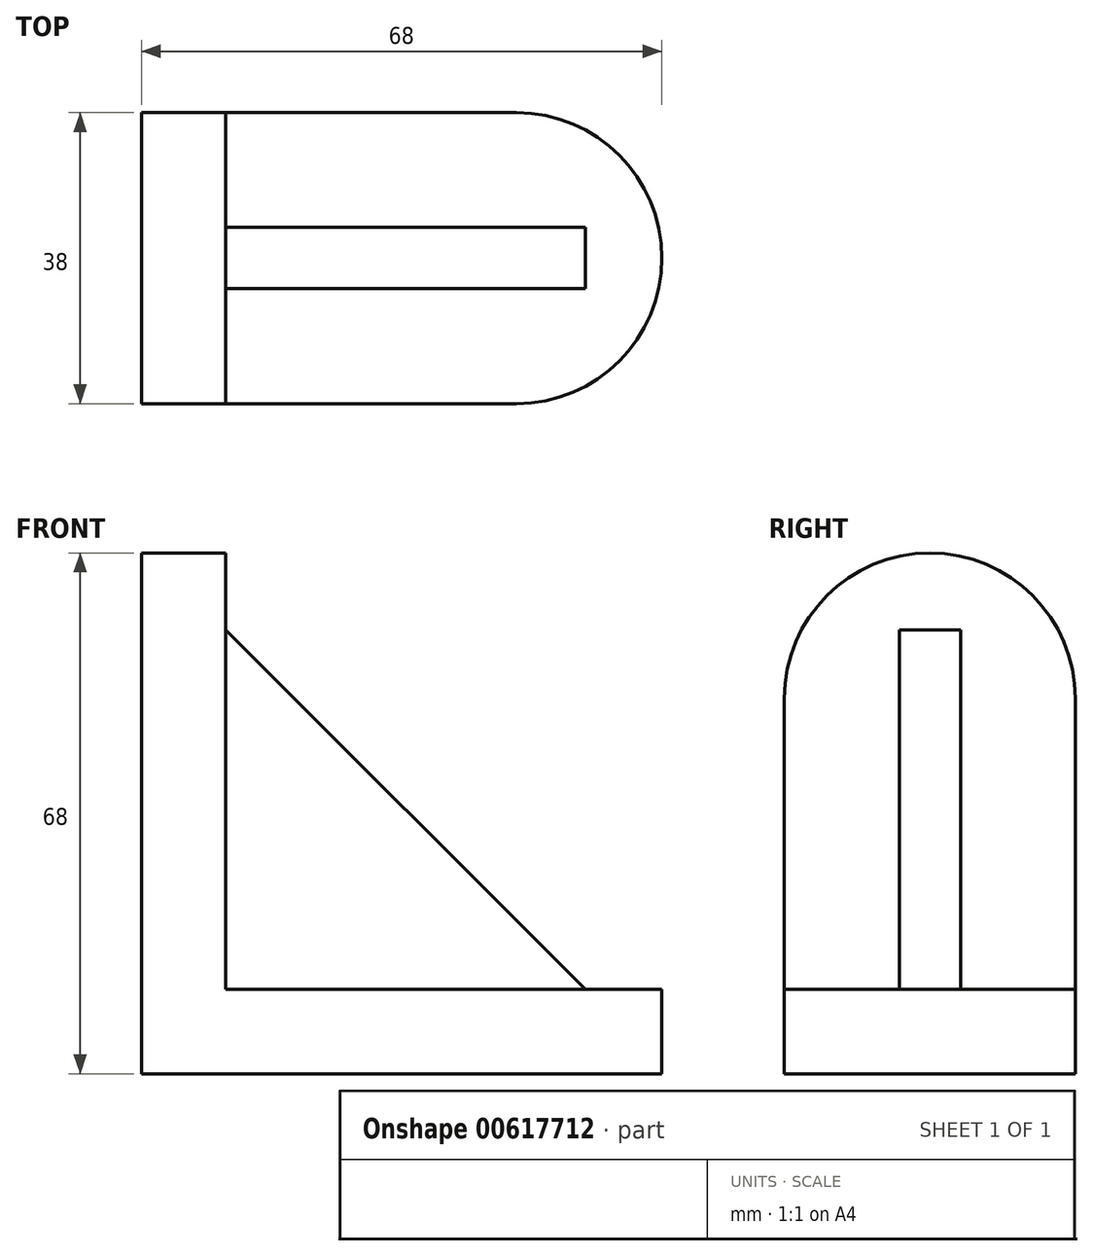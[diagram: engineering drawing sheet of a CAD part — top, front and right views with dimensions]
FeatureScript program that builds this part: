
annotation { "Feature Type Name" : "Feature", "Feature Type Description" : "" }
export const myFeature = defineFeature(function(context is Context, id is Id, definition is map)
    precondition{}
    {
        {
            var Q0;
            Q0=qCreatedBy(makeId("Front.planeOp"),FACE);
            var sketch = newSketch(context, id + "F0", { "sketchPlane" : qUnion([Q0])});
            skLineSegment(sketch, "E0", {"start": v(0, 0) * mm, "end": v(0, 49) * mm});
            skLineSegment(sketch, "E1", {"start": v(0, 49) * mm, "end": v(11, 49) * mm});
            skLineSegment(sketch, "E2", {"start": v(11, 49) * mm, "end": v(11, 11) * mm});
            skLineSegment(sketch, "E3", {"start": v(11, 11) * mm, "end": v(49, 11) * mm});
            skLineSegment(sketch, "E4", {"start": v(49, 11) * mm, "end": v(49, 0) * mm});
            skLineSegment(sketch, "E5", {"start": v(49, 0) * mm, "end": v(0, 0) * mm});
            skSolve(sketch);
        }
        {
            var Q0;
            Q0=makeQuery(id+"F0.imprint","IMPRINT",FACE,{"disambiguationData":[TD([[makeQuery(id+"F0.imprint","IMPRINT",EDGE,{"derivedFrom":sQuery(id+"F0.wireOp",EDGE,"E0")}),-1.0]])]});
            extrude(context, id + "F1", {"entities" : qUnion([Q0]), "depth" : 38 * mm, "offsetDistance" : 25.4 * mm});
        }
        {
            var Q0;
            Q0=makeQuery(id+"F1.opExtrude","SWEPT_FACE",FACE,{"disambiguationData":[OSD([sQuery(id+"F0.wireOp",EDGE,"E0")])]});
            var sketch = newSketch(context, id + "F2", { "sketchPlane" : qUnion([Q0])});
            skArc(sketch, "E6", {"start": v(38, 49) * mm, "mid": v(19, 68) * mm, "end": v(0, 49) * mm});
            skSolve(sketch);
        }
        {
            var Q0;
            Q0=makeQuery(id+"F2.imprint","IMPRINT",FACE,{"disambiguationData":[TD([[makeQuery(id+"F2.imprint","IMPRINT",EDGE,{"derivedFrom":sQuery(id+"F2.wireOp",EDGE,"E6")}),1.0]])]});
            extrude(context, id + "F3", {"entities" : qUnion([Q0]), "operationType" : NewBodyOperationType.ADD, "oppositeDirection" : true, "depth" : 11 * mm, "offsetDistance" : 25.4 * mm});
        }
        {
            var Q0;
            Q0=makeQuery(id+"F1.opExtrude","SWEPT_FACE",FACE,{"disambiguationData":[OSD([sQuery(id+"F0.wireOp",EDGE,"E3")])]});
            var sketch = newSketch(context, id + "F4", { "sketchPlane" : qUnion([Q0])});
            skArc(sketch, "E7", {"start": v(49, -38) * mm, "mid": v(68, -19) * mm, "end": v(49, 0) * mm});
            skSolve(sketch);
        }
        {
            var Q0;
            Q0=makeQuery(id+"F4.imprint","IMPRINT",FACE,{"disambiguationData":[TD([[makeQuery(id+"F4.imprint","IMPRINT",EDGE,{"derivedFrom":sQuery(id+"F4.wireOp",EDGE,"E7")}),1.0]])]});
            extrude(context, id + "F5", {"entities" : qUnion([Q0]), "operationType" : NewBodyOperationType.ADD, "oppositeDirection" : true, "depth" : 11 * mm, "offsetDistance" : 25.4 * mm});
        }
        {
            var Q0;
            Q0=makeQuery(id+"F3.boolean.opBoolean","MERGE",FACE,{"derivedFrom":[makeQuery(id+"F1.opExtrude","SWEPT_FACE",FACE,{"disambiguationData":[OSD([sQuery(id+"F0.wireOp",EDGE,"E2")])]}),makeQuery(id+"F3.opExtrude","CAP_FACE",FACE,{"disambiguationData":[OSD([sQuery(id+"F0.wireOp",EDGE,"E0"),sQuery(id+"F0.wireOp",EDGE,"E1"),sQuery(id+"F2.wireOp",EDGE,"E6")])],"isStart":false})]});
            var sketch = newSketch(context, id + "F6", { "sketchPlane" : qUnion([Q0])});
            skLineSegment(sketch, "E8.bottom", {"start": v(-15, 11) * mm, "end": v(-23, 11) * mm});
            skLineSegment(sketch, "E8.top", {"start": v(-15, 59.49) * mm, "end": v(-23, 59.49) * mm});
            skLineSegment(sketch, "E8.left", {"start": v(-15, 11) * mm, "end": v(-15, 59.49) * mm});
            skLineSegment(sketch, "E8.right", {"start": v(-23, 11) * mm, "end": v(-23, 59.49) * mm});
            skSolve(sketch);
        }
        {
            var Q0;
            Q0 = qSketchRegion(id + "F6", true);
            extrude(context, id + "F7", {"entities" : qUnion([Q0]), "operationType" : NewBodyOperationType.ADD, "depth" : 48.5 * mm, "offsetDistance" : 25.4 * mm});
        }
        {
            var Q0;
            Q0=makeQuery(id+"F7.opExtrude","CAP_EDGE",EDGE,{"disambiguationData":[OSD([sQuery(id+"F6.wireOp",EDGE,"E8.top")])],"isStart":false});
            chamfer(context, id + "F8", {"entities" : qUnion([Q0]), "width" : 50 * mm, "tangentPropagation" : true});
        }
    });
